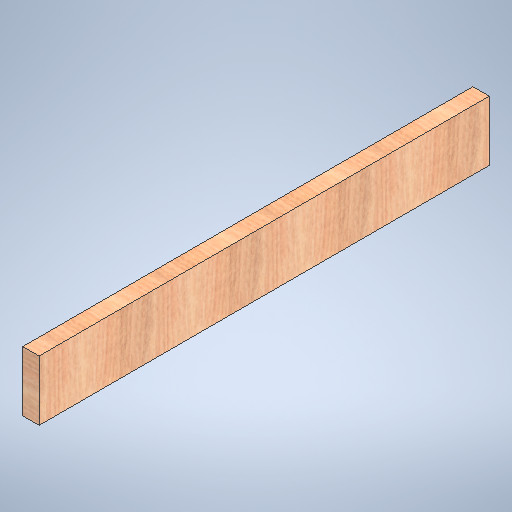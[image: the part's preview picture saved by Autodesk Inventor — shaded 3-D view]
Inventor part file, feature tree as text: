
AUTODESK INVENTOR PART (.ipt)
format: ipt  version: 2025.1 (Build 291241020, 241B)  size: 335,872 bytes
history: native  units: in
note: dims shown in document units (in); Inventor stores cm internally (conversion verified against a paired STEP export)
features: extrude x1, sketch x1
ambient origin geometry x8: Origin, YZ Plane, XZ Plane, XY Plane, X Axis, Y Axis, Z Axis, Center Point
bodies: Solid1 (feature_tree)
feature tree (2):
  extrude  "Extrusion1"  Depth=1.5in TaperAngle=0.0deg
  sketch  "Sketch1"  dims[d1=41.25in d2=1.5in d3=0.0in d4=5.5in]
